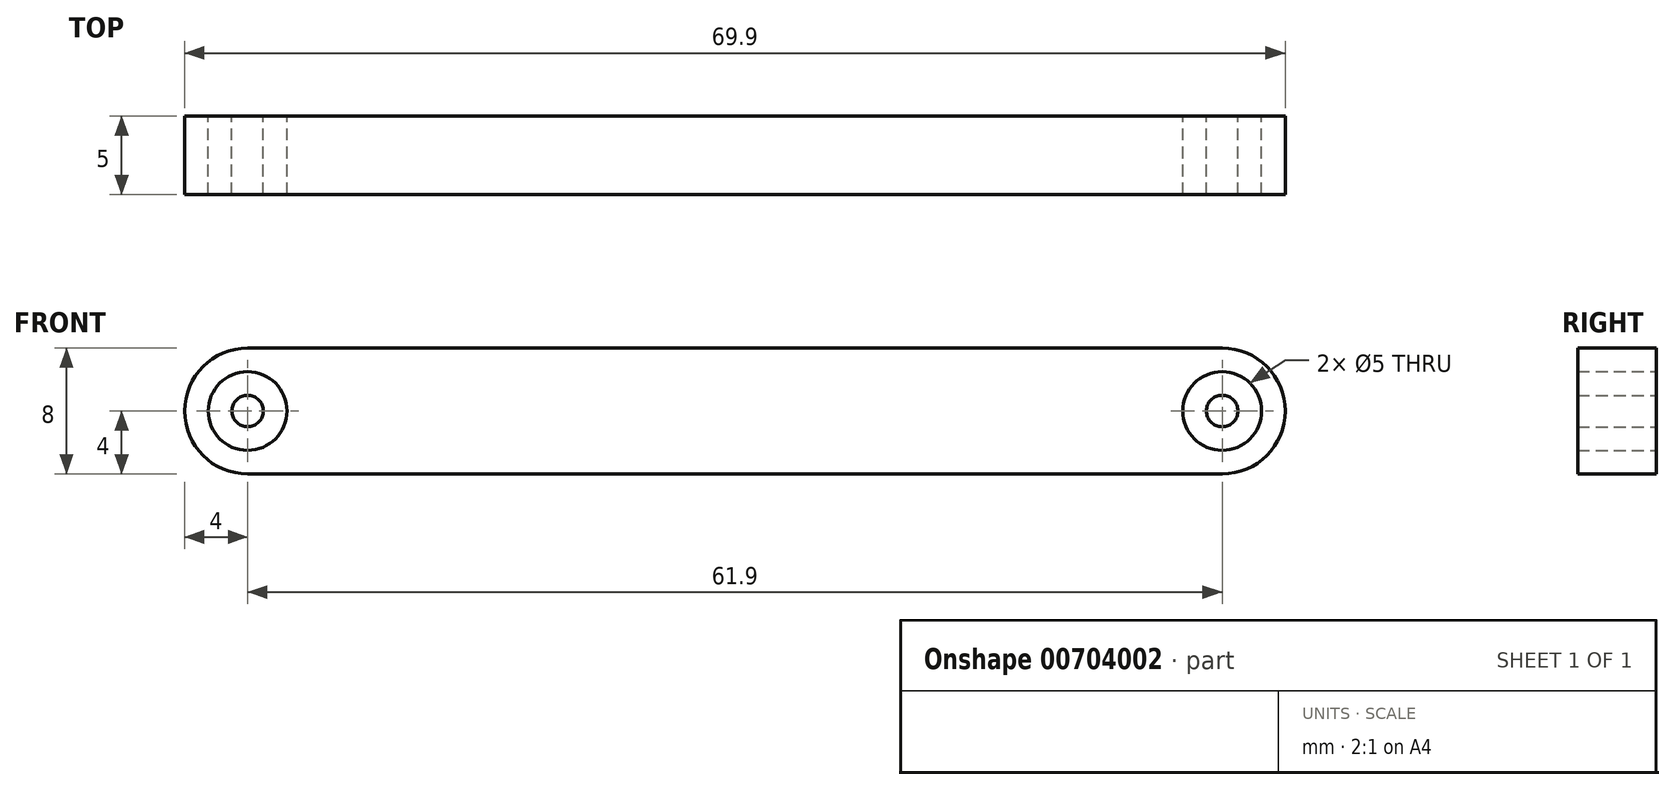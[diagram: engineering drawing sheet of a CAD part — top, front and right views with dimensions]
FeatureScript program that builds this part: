
annotation { "Feature Type Name" : "Feature", "Feature Type Description" : "" }
export const myFeature = defineFeature(function(context is Context, id is Id, definition is map)
    precondition{}
    {
        {
            var Q0;
            Q0=qCreatedBy(makeId("Front.planeOp"),FACE);
            var sketch = newSketch(context, id + "F0", { "sketchPlane" : qUnion([Q0])});
            skLineSegment(sketch, "E0.bottom", {"start": v(0, 0) * mm, "end": v(61.9, 0) * mm});
            skLineSegment(sketch, "E0.top", {"start": v(0, 8) * mm, "end": v(61.9, 8) * mm});
            skArc(sketch, "E1", {"start": v(61.9, 0) * mm, "mid": v(65.9, 4) * mm, "end": v(61.9, 8) * mm});
            skArc(sketch, "E2", {"start": v(0, 8) * mm, "mid": v(-4, 4) * mm, "end": v(0, 0) * mm});
            skCircle(sketch, "E3", {"center": v(0, 4) * mm, "radius": 2.5 * mm});
            skCircle(sketch, "E4", {"center": v(61.9, 4) * mm, "radius": 2.5 * mm});
            skCircle(sketch, "E5", {"center": v(0, 4) * mm, "radius": 1 * mm});
            skCircle(sketch, "E6", {"center": v(61.9, 4) * mm, "radius": 1 * mm});
            skSolve(sketch);
        }
        {
            var Q0;
            Q0 = qSketchRegion(id + "F0", true);
            var Q1;
            Q1=makeQuery(id+"F0.imprint","IMPRINT",FACE,{"disambiguationData":[TD([[makeQuery(id+"F0.imprint","IMPRINT",EDGE,{"derivedFrom":sQuery(id+"F0.wireOp",EDGE,"E5")}),1.0]])]});
            var Q2;
            Q2=makeQuery(id+"F0.imprint","IMPRINT",FACE,{"disambiguationData":[TD([[makeQuery(id+"F0.imprint","IMPRINT",EDGE,{"derivedFrom":sQuery(id+"F0.wireOp",EDGE,"E6")}),1.0]])]});
            extrude(context, id + "F1", {"entities" : qUnion([Q0, Q1, Q2]), "depth" : 5 * mm, "offsetDistance" : 25 * mm});
        }
    });
